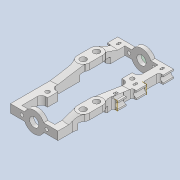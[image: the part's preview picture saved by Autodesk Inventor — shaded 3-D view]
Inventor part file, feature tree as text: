
AUTODESK INVENTOR PART (.ipt)
format: ipt  version: 2020 (Build 240168000, 168)  size: 876,032 bytes
history: native  units: mm
features: projected_geometry x22, sketch x21, extrude x19, thicken_offset x10, chamfer x7, fillet x7, other x5, plane x3, reference x3, hole x2
ambient origin geometry x8: Origin, YZ Plane, XZ Plane, XY Plane, X Axis, Y Axis, Z Axis, Center Point
bodies: Solid1 (feature_tree)
feature tree (99):
  extrude  "Extrusion1"  Depth=4.0mm
  plane  "Work Plane1"
  extrude  "Extrusion2"  Depth=2.0mm TaperAngle=0.0deg
  extrude  "Extrusion3"  Depth=4.0mm
  extrude  "Extrusion4"  Depth=2.0mm TaperAngle=0.0deg
  hole  "Hole1"  [1 undecoded]
  thicken_offset  "Thicken1"
  thicken_offset  "Thicken2"
  thicken_offset  "Thicken3"
  thicken_offset  "Thicken4"
  extrude  "Extrusion5"  Depth=54.0mm
  extrude  "Extrusion6"  Depth=2.0mm
  extrude  "Extrusion8"  Depth=2.0mm
  extrude  "Extrusion9"  Depth=2.0mm
  extrude  "Extrusion11"  Depth=3.5mm
  hole  "Hole2"  [1 undecoded]
  extrude  "Extrusion15"  Depth=3.5mm
  extrude  "Extrusion16"  Depth=7.5mm
  chamfer  "Chamfer1"  Distance=6.5mm
  chamfer  "Chamfer2"  Distance=6.0mm
  chamfer  "Chamfer3"  Distance=2.0mm
  chamfer  "Chamfer4"  Distance=7.5mm
  fillet  "Fillet4"  Radius=9.0mm
  fillet  "Fillet5"  Radius=2.0mm
  chamfer  "Chamfer5"  Distance=3.25mm
  fillet  "Fillet6"  Radius=6.5mm
  extrude  "Extrusion17"  Depth=1.0mm
  plane  "Work Plane3"
  extrude  "Extrusion18"  Depth=2.0mm TaperAngle=0.0deg
  plane  "Work Plane4"
  extrude  "Extrusion19"  Depth=1.0mm
  extrude  "Extrusion20"  Depth=1.0mm TaperAngle=0.0deg
  fillet  "Fillet8"  Radius=3.0mm
  fillet  "Fillet9"  Radius=3.0mm
  fillet  "Fillet10"  Radius=3.0mm
  extrude  "Extrusion21"  Depth=1.0mm
  extrude  "Extrusion22"  Depth=1.0mm
  thicken_offset  "Thicken9"
  thicken_offset  "Thicken10"
  thicken_offset  "Thicken11"
  thicken_offset  "Thicken12"
  extrude  "Extrusion23"  Depth=1.0mm TaperAngle=0.0deg
  fillet  "Fillet11"  Radius=6.0mm
  extrude  "Extrusion24"  Depth=2.0mm TaperAngle=0.0deg
  thicken_offset  "Thicken13"
  thicken_offset  "Thicken14"
  chamfer  "Chamfer7"  Distance=6.0mm
  chamfer  "Chamfer8"  Distance=2.0mm
  sketch  "Sketch1"  dims[d0=10.0mm d1=4.0mm]
  sketch  "Sketch2"  dims[d2=30.0mm d3=2.0mm d4=0.0mm]
  sketch  "Sketch3"  dims[d5=10.0mm d6=4.0mm]
  projected_geometry  "Projected Loop1"
  projected_geometry  "Projected Loop2"
  projected_geometry  "Projected Loop3"
  projected_geometry  "Projected Loop4"
  sketch  "Sketch4"  dims[d7=30.0mm d8=2.0mm d9=0.0mm]
  sketch  "Sketch5"  dims[d10=3.0mm d11=54.0mm]
  sketch  "Sketch6"  dims[d12=3.0mm d13=54.0mm]
  projected_geometry  "Projected Loop5"
  reference  "Reference1"
  reference  "Reference2"
  sketch  "Sketch7"  dims[d14=2.0mm d15=0.0mm d16=4.5mm]
  projected_geometry  "Projected Loop6"
  reference  "Reference3"
  sketch  "Sketch9"  dims[d17=2.0mm d18=0.0mm d19=6.0mm]
  projected_geometry  "Projected Loop9"
  sketch  "Sketch10"  dims[d20=6.0mm]
  projected_geometry  "Projected Loop10"
  sketch  "Sketch12"  dims[d21=1.6mm d22=6.0mm d23=4.0mm d24=2.0mm d25=90.0deg d26=100.0mm d27=0.0mm d28=3.5mm]
  projected_geometry  "Projected Loop13"
  sketch  "Sketch13"  dims[d29=3.5mm d30=3.5mm]
  projected_geometry  "Projected Loop14"
  sketch  "Sketch18"  dims[d31=3.5mm d32=3.5mm]
  projected_geometry  "Projected Loop20"
  sketch  "Sketch19"  dims[d33=3.5mm d34=3.5mm]
  projected_geometry  "Projected Loop21"
  sketch  "Sketch20"  dims[d35=3.5mm d36=7.5mm]
  projected_geometry  "Projected Loop22"
  sketch  "Sketch21"  dims[d37=9.0mm]
  projected_geometry  "Projected Loop23"
  sketch  "Sketch22"  dims[d38=3.0mm]
  projected_geometry  "Projected Loop24"
  sketch  "Sketch23"  dims[d39=3.25mm]
  projected_geometry  "Projected Loop25"
  sketch  "Sketch24"  dims[d40=3.25mm]
  projected_geometry  "Projected Loop26"
  sketch  "Sketch25"  dims[d41=6.0mm]
  projected_geometry  "Projected Loop27"
  sketch  "Sketch26"  dims[d42=6.0mm]
  projected_geometry  "Projected Loop28"
  projected_geometry  "Projected Loop29"
  sketch  "Sketch27"  dims[d43=2.0mm d44=6.5mm d45=6.0mm d46=2.0mm d47=0.0mm d48=7.5mm d49=9.0mm d50=2.0mm d51=3.25mm d52=6.5mm d53=6.0mm d54=2.0mm d55=0.0mm d60=7.0mm d61=3.0mm d62=0.0mm d66=3.0mm d67=3.0mm d68=3.0mm d69=0.0mm d76=6.5mm d77=7.0mm d78=3.0mm d79=0.0mm d80=3.0mm d81=6.0mm d82=4.0mm d83=2.0mm d84=90.0deg d85=100.0mm d86=0.0mm d107=6.0mm d108=2.0mm d109=0.0mm d110=6.0mm d111=2.0mm d112=0.0mm d113=12.0mm d114=2.0mm d115=30.0deg d116=5.0mm d117=2.0mm d118=30.0deg d119=12.0mm d120=2.0mm d121=30.0deg d122=5.0mm d123=2.0mm d124=30.0deg d125=1.0mm d126=8.0mm d127=1.0mm d128=2.0mm d129=30.0deg d130=0.5mm d135=2.5mm d136=2.0mm d137=4.0mm d138=5.0mm d139=0.0mm d140=8.0mm d141=5.0mm d142=0.0mm d143=9.0mm d144=4.0mm d145=0.0mm d146=2.5mm d147=2.0mm d148=4.0mm d149=5.0mm d150=0.0mm d151=1.0mm d152=1.0mm d153=1.0mm d154=3.0mm d155=2.0mm d156=3.0mm d157=2.0mm d158=3.0mm d159=2.0mm d160=0.5mm d161=1.0mm d162=0.5mm d163=1.0mm d164=0.5mm d165=1.0mm d166=8.0mm d167=0.0mm d168=3.0mm d169=0.5mm d170=1.0mm d171=8.0mm d172=0.0mm d173=0.5mm d174=0.5mm d175=0.5mm d176=0.5mm d177=0.5mm d178=0.5mm d179=0.5mm d180=0.5mm d181=12.0mm d182=1.5mm d183=3.0mm d184=5.0mm d185=12.0mm d186=1.5mm d187=3.0mm d188=5.0mm d189=8.0mm d190=0.0mm d191=2.0mm d192=2.5mm d193=2.0mm d194=2.5mm d195=2.0mm d196=8.0mm d197=0.0mm d198=1.0mm d199=1.0mm d200=1.0mm d201=1.0mm d202=1.0mm d203=6.0mm d204=30.0deg d205=1.0mm d206=6.0mm d207=30.0deg]
  projected_geometry  "Projected Loop30"
  projected_geometry  "Projected Loop31"
  parser-record x1  (decoder bookkeeping rows leaked as tree rows — omitted from the tree; the rows remain in map.json)
  other  "tip2_ass_t1.iam"
  other  "cab_coil_1:1"
  other  "cab_coil_1:2"
  other  "bearing_3_6_2:1"
note: 2 required parameter values undecoded (feature->parameter linkage not recoverable at this tier; creation-order binding heuristic only, values carry confidence <= 0.55)
note: 1 file-system path scrubbed to <path> (originals preserved in map.json)
